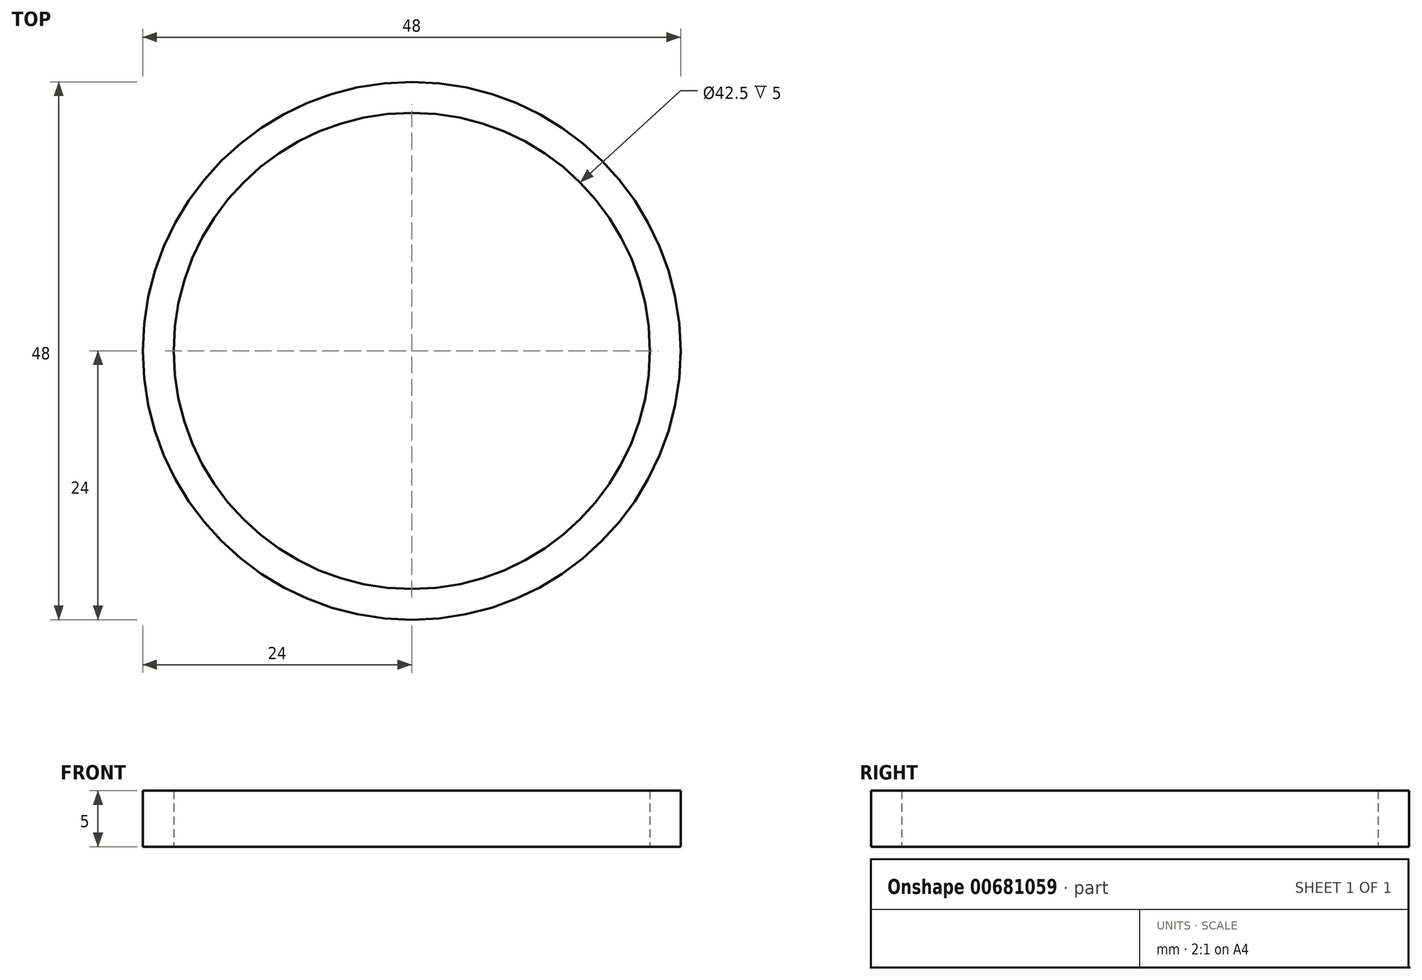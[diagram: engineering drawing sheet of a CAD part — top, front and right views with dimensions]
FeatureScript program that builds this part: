
annotation { "Feature Type Name" : "Feature", "Feature Type Description" : "" }
export const myFeature = defineFeature(function(context is Context, id is Id, definition is map)
    precondition{}
    {
        {
            var Q0;
            Q0=qCreatedBy(makeId("Top.planeOp"),FACE);
            var sketch = newSketch(context, id + "F0", { "sketchPlane" : qUnion([Q0])});
            skCircle(sketch, "E0", {"center": v(0, 0) * mm, "radius": 21.25 * mm});
            skCircle(sketch, "E1", {"center": v(0, 0) * mm, "radius": 24 * mm});
            skSolve(sketch);
        }
        {
            var Q0;
            Q0 = qSketchRegion(id + "F0", true);
            extrude(context, id + "F1", {"entities" : qUnion([Q0]), "depth" : 5 * mm, "offsetDistance" : 25 * mm});
        }
    });
